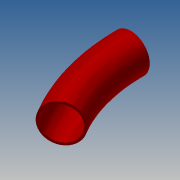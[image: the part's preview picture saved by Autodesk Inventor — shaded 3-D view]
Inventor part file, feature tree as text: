
AUTODESK INVENTOR PART (.ipt)
format: ipt  version: 2017.3 (Build 213257000, 257)  size: 144,384 bytes
history: native  units: in
note: dims shown in document units (in); Inventor stores cm internally (conversion verified against a paired STEP export)
features: other x3, revolve x1, sketch x1
ambient origin geometry x8: Origin, YZ Plane, XZ Plane, XY Plane, X Axis, Y Axis, Z Axis, Center Point
bodies: Solid1 (feature_tree)
feature tree (5):
  other  "A1-19027-100-05 HCWI elbow - female.ipt"
  revolve  "Revolution1"  [1 undecoded]
  other  "Solid1::A1-19027-100-05 HCWI elbow - female.ipt"
  other  "TaggingFeature1"
  sketch  "Sketch1"  dims[d0=0.3937in d1=0.213in]
note: 1 required parameter value undecoded (feature->parameter linkage not recoverable at this tier; creation-order binding heuristic only, values carry confidence <= 0.55)
